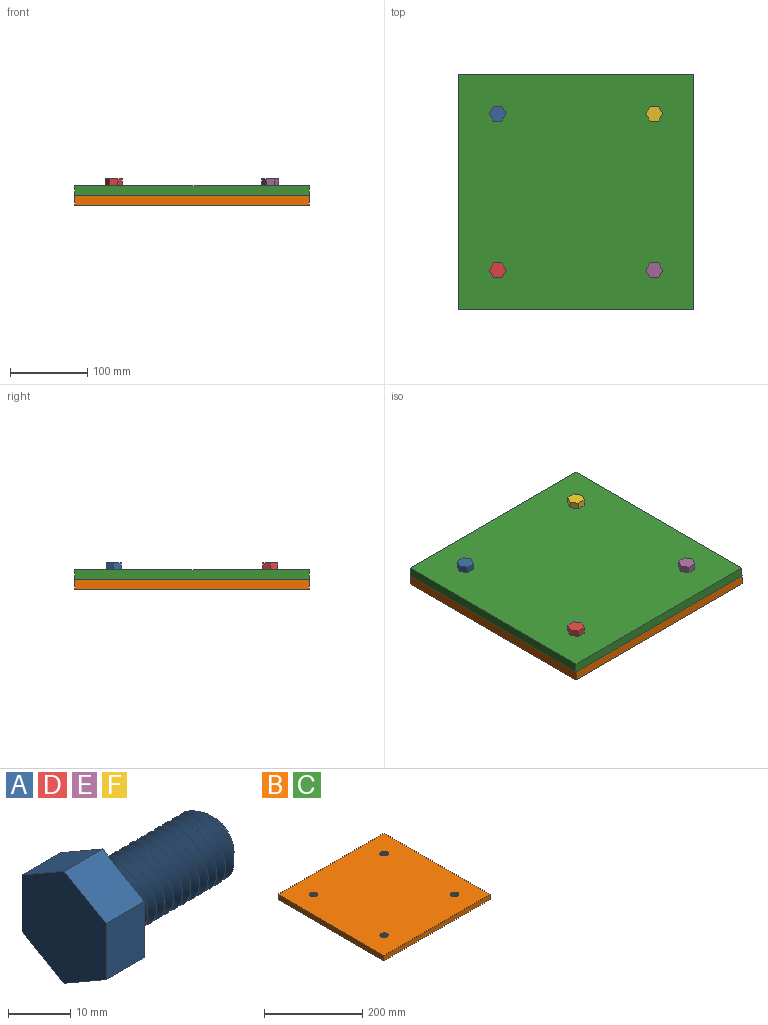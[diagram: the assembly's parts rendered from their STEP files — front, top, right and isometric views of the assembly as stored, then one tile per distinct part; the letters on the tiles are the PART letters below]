
ASSEMBLY  parts=6 mates=5
PART A: 14 faces, bbox 35.1x19.1x22 mm
  f0: cylinder r=6.35mm len=23.45mm, axis (-1,0,0), area 133.2mm2, adj f2,f3,f4,f5,f6
  f1: plane 8.79x8.79mm, normal (1,0,0), area 60.7mm2, adj f2
  f2: cone r=6.35mm half-angle=45deg, axis (-1,0,0), area 50.8mm2, adj f0,f1,f4,f5
  f3: plane 1.93x1.67mm, normal (0,0,-1), area 1.6mm2, adj f0,f4,f5
  f4: bspline ~25.39x14.66mm, area 782.1mm2, adj f0,f2,f3,f5
  f5: bspline ~25.39x14.66mm, area 817mm2, adj f0,f2,f3,f4
  f6: plane 22x19.05mm, normal (1,0,0), area 187.6mm2, adj f0,f7,f8,f9,f10,f11,f12
  f7: plane 9.53x8.73mm, normal (0,-0.5,0.87), area 96mm2, adj f6,f8,f12,f13
  f8: plane 9.53x8.73mm, normal (0,0.5,0.87), area 96mm2, adj f6,f7,f9,f13
  f9: plane 11x8.73mm, normal (0,1,0), area 96mm2, adj f6,f8,f10,f13
  f10: plane 9.53x8.73mm, normal (0,0.5,-0.87), area 96mm2, adj f6,f9,f11,f13
  f11: plane 9.53x8.73mm, normal (0,-0.5,-0.87), area 96mm2, adj f6,f10,f12,f13
  f12: plane 11x8.73mm, normal (0,-1,0), area 96mm2, adj f6,f7,f11,f13
  f13: plane 22x19.05mm, normal (-1,0,0), area 314.3mm2, adj f7,f8,f9,f10,f11,f12
PART B: 18 faces, bbox 306.2x306.2x16.3 mm
  f0: cylinder r=7.01mm len=14.02mm, axis (0,0,-1), area 6.9mm2, adj f8,f9,f16,f17
  f1: cylinder r=7.01mm len=14.02mm, axis (0,0,-1), area 6.9mm2, adj f8,f9,f14,f15
  f2: cylinder r=7.01mm len=14.02mm, axis (0,0,-1), area 6.9mm2, adj f8,f9,f12,f13
  f3: cylinder r=7.01mm len=14.02mm, axis (0,0,-1), area 6.9mm2, adj f8,f9,f10,f11
  f4: plane 304.8x12.7mm, normal (0,1,0), area 3871mm2, adj f5,f7,f8,f9
  f5: plane 304.8x12.7mm, normal (-1,0,0), area 3871mm2, adj f4,f6,f8,f9
  f6: plane 304.8x12.7mm, normal (0,-1,0), area 3871mm2, adj f5,f7,f8,f9
  f7: plane 304.8x12.7mm, normal (1,0,0), area 3871mm2, adj f4,f6,f8,f9
  f8: plane 306.16x306.16mm, normal (0,0,1), area 92127.3mm2, adj f0,f1,f2,f3,f4,f5,f6,f7
  f9: plane 306.16x306.16mm, normal (0,0,-1), area 92129.4mm2, adj f0,f1,f2,f3,f4,f5,f6,f7
  f10: bspline ~20.05x17.36mm, area 622.6mm2, adj f3,f8,f9,f11
  f11: bspline ~20.05x17.36mm, area 622.5mm2, adj f3,f8,f9,f10
  f12: bspline ~20.05x17.36mm, area 622.6mm2, adj f2,f8,f9,f13
  f13: bspline ~20.05x17.36mm, area 622.5mm2, adj f2,f8,f9,f12
  f14: bspline ~20.05x17.36mm, area 622.6mm2, adj f1,f8,f9,f15
  f15: bspline ~20.05x17.36mm, area 622.5mm2, adj f1,f8,f9,f14
  f16: bspline ~20.05x17.36mm, area 622.6mm2, adj f0,f8,f9,f17
  f17: bspline ~20.05x17.36mm, area 622.5mm2, adj f0,f8,f9,f16
PART C: same geometry as B
PART D: same geometry as A
PART E: same geometry as A
PART F: same geometry as A
PLACE A rot(axis=(0.71,0,-0.71),180deg) t=(-100.71,101.62,69.11)mm
PLACE B t=(0.9,0.02,-7.09)mm
PLACE C t=(0.89,0.02,5.61)mm
PLACE D rot(axis=(0.71,0,-0.71),180deg) t=(-100.71,-101.58,69.11)mm
PLACE E rot(axis=(0.71,0,-0.71),180deg) t=(102.49,-101.58,69.11)mm
PLACE F rot(axis=(0.71,0,-0.71),180deg) t=(102.49,101.62,69.11)mm
MATE fastened E.f0 <-> C.f0  axis (0,0,-1) through (102.49,-101.58,18.31)mm
MATE fastened A.f0 <-> C.f2  axis (0,0,-1) through (-100.71,101.62,18.31)mm
MATE fastened F.f0 <-> C.f3  axis (0,0,-1) through (102.49,101.62,18.31)mm
MATE fastened D.f0 <-> C.f1  axis (0,0,-1) through (-100.71,-101.58,18.31)mm
MATE fastened C.f9 <-> B.f8  axis (0,0,-1) through (0.9,0.02,5.61)mm
